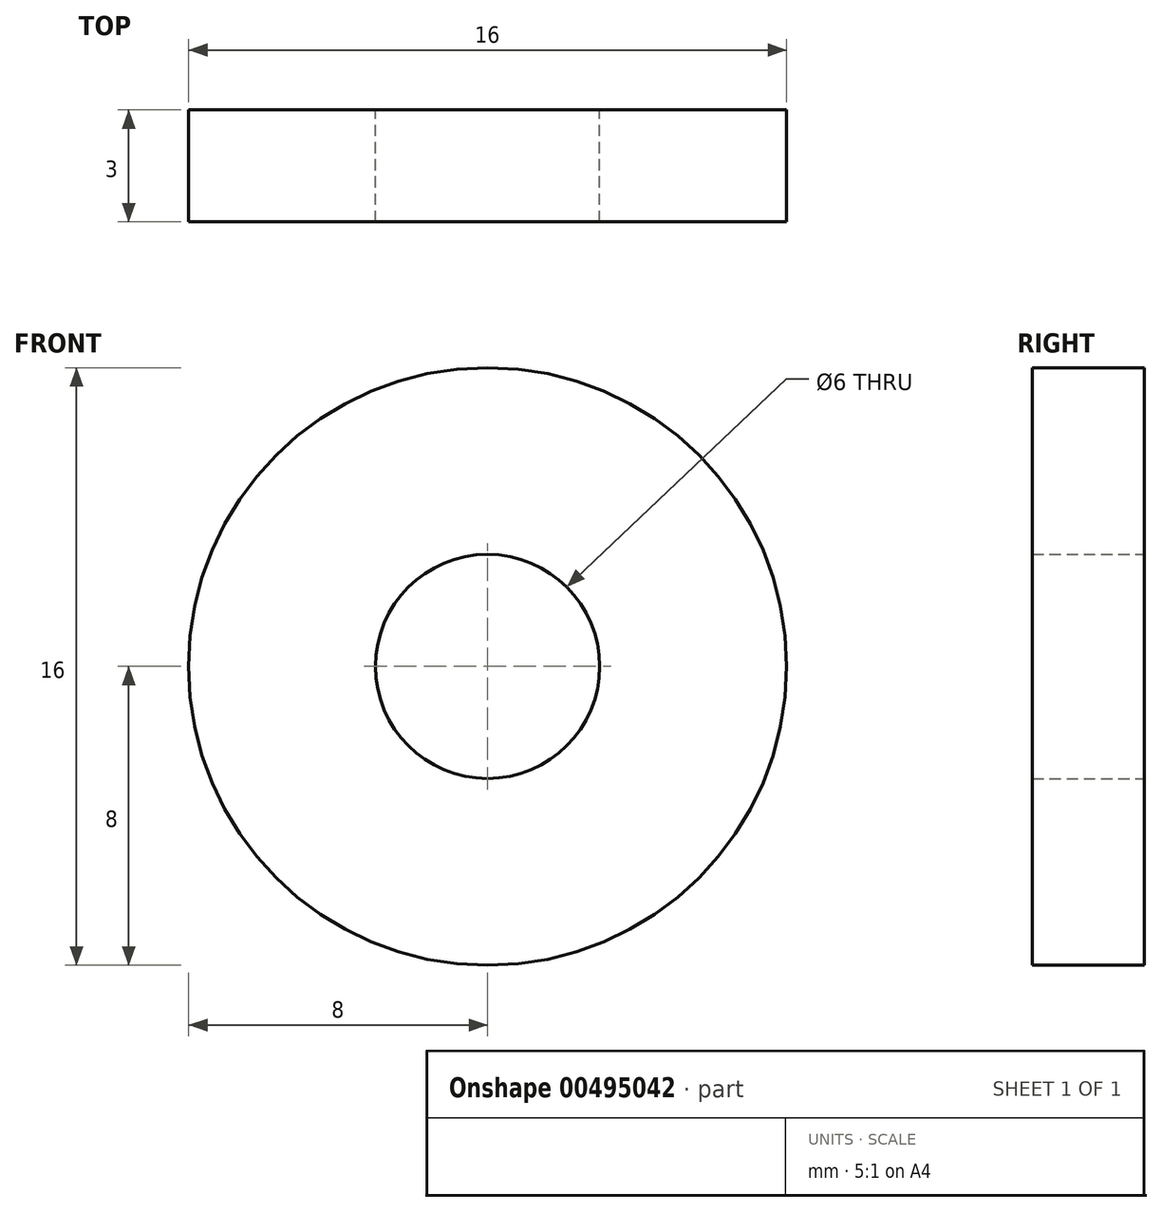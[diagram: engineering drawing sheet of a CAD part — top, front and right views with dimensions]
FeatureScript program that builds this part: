
annotation { "Feature Type Name" : "Feature", "Feature Type Description" : "" }
export const myFeature = defineFeature(function(context is Context, id is Id, definition is map)
    precondition{}
    {
        {
            var Q0;
            Q0=qCreatedBy(makeId("Front.planeOp"),FACE);
            var sketch = newSketch(context, id + "F0", { "sketchPlane" : qUnion([Q0])});
            skCircle(sketch, "E0", {"center": v(0, 0) * mm, "radius": 8 * mm});
            skCircle(sketch, "E1", {"center": v(0, 0) * mm, "radius": 3 * mm});
            skSolve(sketch);
        }
        {
            var Q0;
            Q0 = qSketchRegion(id + "F0", true);
            extrude(context, id + "F1", {"entities" : qUnion([Q0]), "depth" : 3 * mm});
        }
    });
